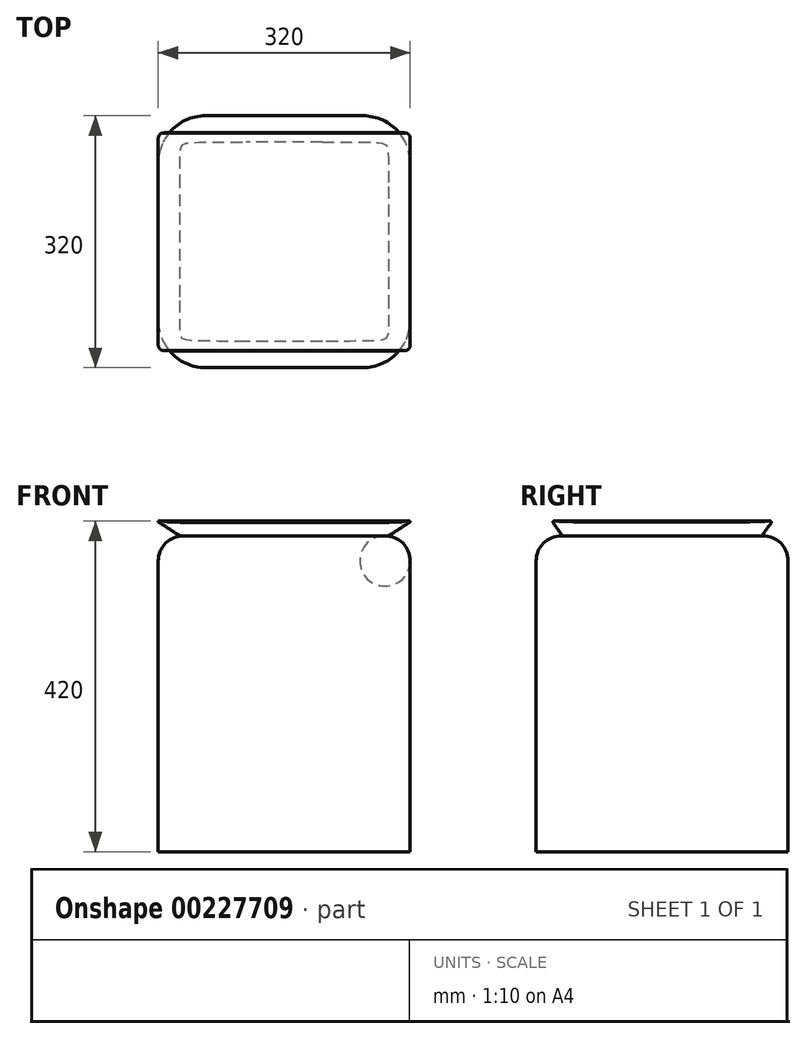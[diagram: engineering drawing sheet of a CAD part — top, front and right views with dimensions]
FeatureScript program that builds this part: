
annotation { "Feature Type Name" : "Feature", "Feature Type Description" : "" }
export const myFeature = defineFeature(function(context is Context, id is Id, definition is map)
    precondition{}
    {
        {
            var Q0;
            Q0=qCreatedBy(makeId("Right.planeOp"),FACE);
            var sketch = newSketch(context, id + "F0", { "sketchPlane" : qUnion([Q0])});
            skLineSegment(sketch, "E0", {"start": v(-172.62, -274.52) * mm, "end": v(-172.62, 126.84) * mm});
            skLineSegment(sketch, "E1", {"start": v(-172.62, 126.84) * mm, "end": v(-139.2, 126.84) * mm});
            skLineSegment(sketch, "E2", {"start": v(-139.2, 126.84) * mm, "end": v(-152.62, 108.2) * mm});
            skLineSegment(sketch, "E3", {"start": v(-152.62, 108.2) * mm, "end": v(127.38, 108.2) * mm});
            skLineSegment(sketch, "E4", {"start": v(127.38, 108.2) * mm, "end": v(113.96, 126.84) * mm});
            skLineSegment(sketch, "E5", {"start": v(113.96, 126.84) * mm, "end": v(147.38, 126.84) * mm});
            skLineSegment(sketch, "E6", {"start": v(147.38, 126.84) * mm, "end": v(147.38, -274.52) * mm});
            skLineSegment(sketch, "E7", {"start": v(147.38, -274.52) * mm, "end": v(-172.62, -274.52) * mm});
            skLineSegment(sketch, "E8", {"start": v(-12.62, 108.2) * mm, "end": v(-12.62, -274.52) * mm, "construction": true});
            skLineSegment(sketch, "E9", {"start": v(-139.2, 126.84) * mm, "end": v(113.96, 126.84) * mm});
            skLineSegment(sketch, "E10.MirrorCS", {"start": v(127.38, 145.48) * mm, "end": v(113.96, 126.84) * mm});
            skLineSegment(sketch, "E11.MirrorCS", {"start": v(-139.2, 126.84) * mm, "end": v(-152.62, 145.48) * mm});
            skLineSegment(sketch, "E12.MirrorCS", {"start": v(-152.62, 145.48) * mm, "end": v(127.38, 145.48) * mm});
            skSolve(sketch);
        }
        {
            var Q0;
            Q0=makeQuery(id+"F0.imprint","IMPRINT",FACE,{"disambiguationData":[TD([[makeQuery(id+"F0.imprint","IMPRINT",EDGE,{"derivedFrom":sQuery(id+"F0.wireOp",EDGE,"E0")}),-1.0]])]});
            var Q1;
            Q1=makeQuery(id+"F0.imprint","IMPRINT",FACE,{"disambiguationData":[TD([[makeQuery(id+"F0.imprint","IMPRINT",EDGE,{"derivedFrom":sQuery(id+"F0.wireOp",EDGE,"E2")}),1.0]])]});
            extrude(context, id + "F1", {"entities" : qUnion([Q0, Q1]), "depth" : 320 * mm, "symmetric" : true});
        }
        {
            var Q0;
            Q0=makeQuery(id+"F0.imprint","IMPRINT",FACE,{"disambiguationData":[TD([[makeQuery(id+"F0.imprint","IMPRINT",EDGE,{"derivedFrom":sQuery(id+"F0.wireOp",EDGE,"E9")}),1.0]])]});
            extrude(context, id + "F2", {"entities" : qUnion([Q0]), "depth" : 320 * mm, "symmetric" : true});
        }
        {
            var Q0;
            Q0=makeQuery(id+"F1.opExtrude","CAP_EDGE",EDGE,{"disambiguationData":[OSD([sQuery(id+"F0.wireOp",EDGE,"E6")])],"isStart":false});
            var Q1;
            Q1=makeQuery(id+"F1.opExtrude","CAP_EDGE",EDGE,{"disambiguationData":[OSD([sQuery(id+"F0.wireOp",EDGE,"E6")])],"isStart":true});
            var Q2;
            Q2=makeQuery(id+"F1.opExtrude","CAP_EDGE",EDGE,{"disambiguationData":[OSD([sQuery(id+"F0.wireOp",EDGE,"E0")])],"isStart":false});
            var Q3;
            Q3=makeQuery(id+"F1.opExtrude","CAP_EDGE",EDGE,{"disambiguationData":[OSD([sQuery(id+"F0.wireOp",EDGE,"E0")])],"isStart":true});
            fillet(context, id + "F3", {"entities" : qUnion([Q0, Q1, Q2, Q3]), "radius" : 60 * mm, "tangentPropagation" : true, "allowEdgeOverflow" : false});
        }
        {
            var Q0;
            Q0=makeQuery(id+"F1.opExtrude","SWEPT_EDGE",EDGE,{"disambiguationData":[OSD([sQuery(id+"F0.wireOp",EDGE,"E5"),sQuery(id+"F0.wireOp",EDGE,"E6")])]});
            var Q1;
            Q1=makeQuery(id+"F1.opExtrude","SWEPT_EDGE",EDGE,{"disambiguationData":[OSD([sQuery(id+"F0.wireOp",EDGE,"E0"),sQuery(id+"F0.wireOp",EDGE,"E1")])]});
            var Q2;
            Q2=makeQuery(id+"F1.opExtrude","CAP_EDGE",EDGE,{"disambiguationData":[OSD([sQuery(id+"F0.wireOp",EDGE,"E5")])],"isStart":false});
            var Q3;
            Q3=makeQuery(id+"F1.opExtrude","CAP_EDGE",EDGE,{"disambiguationData":[OSD([sQuery(id+"F0.wireOp",EDGE,"E1")])],"isStart":false});
            var Q4;
            Q4=makeQuery(id+"F1.opExtrude","CAP_EDGE",EDGE,{"disambiguationData":[OSD([sQuery(id+"F0.wireOp",EDGE,"E5")])],"isStart":true});
            var Q5;
            Q5=makeQuery(id+"F1.opExtrude","CAP_EDGE",EDGE,{"disambiguationData":[OSD([sQuery(id+"F0.wireOp",EDGE,"E1")])],"isStart":true});
            fillet(context, id + "F4", {"entities" : qUnion([Q0, Q1, Q2, Q3, Q4, Q5]), "radius" : 32 * mm, "tangentPropagation" : true, "allowEdgeOverflow" : false});
        }
        {
            var Q0;
            Q0=makeQuery(id+"F2.opExtrude","SWEPT_EDGE",EDGE,{"disambiguationData":[OSD([sQuery(id+"F0.wireOp",EDGE,"E10.MirrorCS"),sQuery(id+"F0.wireOp",EDGE,"E12.MirrorCS")])]});
            var Q1;
            Q1=makeQuery(id+"F2.opExtrude","SWEPT_EDGE",EDGE,{"disambiguationData":[OSD([sQuery(id+"F0.wireOp",EDGE,"E11.MirrorCS"),sQuery(id+"F0.wireOp",EDGE,"E12.MirrorCS")])]});
            chamfer(context, id + "F5", {"entities" : qUnion([Q0, Q1]), "width" : 1 * mm, "tangentPropagation" : true});
        }
        {
            var Q0;
            Q0=makeQuery(id+"F2.opExtrude","CAP_EDGE",EDGE,{"disambiguationData":[OSD([sQuery(id+"F0.wireOp",EDGE,"E9")])],"isStart":false});
            var Q1;
            Q1=makeQuery(id+"F2.opExtrude","CAP_EDGE",EDGE,{"disambiguationData":[OSD([sQuery(id+"F0.wireOp",EDGE,"E9")])],"isStart":true});
            chamfer(context, id + "F6", {"entities" : qUnion([Q0, Q1]), "chamferType" : ChamferType.OFFSET_ANGLE, "width" : 17.8 * mm, "oppositeDirection" : false, "angle" : 57 * degree, "tangentPropagation" : true});
        }
        {
            var Q0;
            Q0=makeQuery(id+"F2.opExtrude","SWEPT_FACE",FACE,{"disambiguationData":[OSD([sQuery(id+"F0.wireOp",EDGE,"E12.MirrorCS")])]});
            var sketch = newSketch(context, id + "F7", { "sketchPlane" : qUnion([Q0])});
            skLineSegment(sketch, "E13.0.0", {"start": v(-160, 126.38) * mm, "end": v(-160, -151.62) * mm});
            skLineSegment(sketch, "E13.0.1", {"start": v(-160, -151.62) * mm, "end": v(160, -151.62) * mm});
            skLineSegment(sketch, "E13.0.2", {"start": v(160, -151.62) * mm, "end": v(160, 126.38) * mm});
            skLineSegment(sketch, "E13.0.3", {"start": v(160, 126.38) * mm, "end": v(-160, 126.38) * mm});
            skSolve(sketch);
        }
        {
            var Q0;
            Q0=makeQuery(id+"F1.opExtrude","SWEPT_FACE",FACE,{"disambiguationData":[OSD([sQuery(id+"F0.wireOp",EDGE,"E1"),sQuery(id+"F0.wireOp",EDGE,"E5"),sQuery(id+"F0.wireOp",EDGE,"E9")])]});
            var sketch = newSketch(context, id + "F8", { "sketchPlane" : qUnion([Q0])});
            skArc(sketch, "E14.0.0", {"start": v(100, -140.62) * mm, "mid": v(119.8, -132.42) * mm, "end": v(128, -112.62) * mm});
            skLineSegment(sketch, "E14.0.1", {"start": v(128, -112.62) * mm, "end": v(128, 87.38) * mm});
            skArc(sketch, "E14.0.2", {"start": v(128, 87.38) * mm, "mid": v(119.8, 107.18) * mm, "end": v(100, 115.38) * mm});
            skLineSegment(sketch, "E14.0.3", {"start": v(100, 115.38) * mm, "end": v(-100, 115.38) * mm});
            skArc(sketch, "E14.0.4", {"start": v(-100, 115.38) * mm, "mid": v(-119.8, 107.18) * mm, "end": v(-128, 87.38) * mm});
            skLineSegment(sketch, "E14.0.5", {"start": v(-128, 87.38) * mm, "end": v(-128, -112.62) * mm});
            skArc(sketch, "E14.0.6", {"start": v(-128, -112.62) * mm, "mid": v(-119.8, -132.42) * mm, "end": v(-100, -140.62) * mm});
            skLineSegment(sketch, "E14.0.7", {"start": v(-100, -140.62) * mm, "end": v(100, -140.62) * mm});
            skSolve(sketch);
        }
        {
            var Q0;
            Q0=sQuery(id+"F8.wireOp",EDGE,"E14.0.0");
            cPoint(context, id + "F9", {"entities" : qUnion([Q0]), "parameter" : 0.5});
        }
        {
            var Q0;
            Q0 = qCreatedBy(id + "F9" ,VERTEX);
            var Q1;
            Q1=sQuery(id+"F7.wireOp",VERTEX,"E13.0.2.start");
            var Q2;
            Q2=sQuery(id+"F7.wireOp",VERTEX,"E13.0.0.start");
            cPlane(context, id + "F10", {"entities" : qUnion([Q0, Q1, Q2]), "cplaneType" : CPlaneType.THREE_POINT, "offset" : 25 * mm, "width" : 150 * mm, "height" : 150 * mm});
        }
        {
            var Q0;
            Q0=makeQuery(id+"F6.opChamfer","BLEND_EDGE",EDGE,{"blendedFrom":[makeQuery(id+"F2.opExtrude","CAP_EDGE",EDGE,{"disambiguationData":[OSD([sQuery(id+"F0.wireOp",EDGE,"E9")])],"isStart":false}),makeQuery(id+"F2.opExtrude","SWEPT_FACE",FACE,{"disambiguationData":[OSD([sQuery(id+"F0.wireOp",EDGE,"E11.MirrorCS")])]})],"blendedInto":[makeQuery(id+"F2.opExtrude","SWEPT_FACE",FACE,{"disambiguationData":[OSD([sQuery(id+"F0.wireOp",EDGE,"E11.MirrorCS")])]})]});
            var Q1;
            Q1=makeQuery(id+"F6.opChamfer","BLEND_EDGE",EDGE,{"blendedFrom":[makeQuery(id+"F2.opExtrude","CAP_EDGE",EDGE,{"disambiguationData":[OSD([sQuery(id+"F0.wireOp",EDGE,"E9")])],"isStart":false}),makeQuery(id+"F2.opExtrude","SWEPT_FACE",FACE,{"disambiguationData":[OSD([sQuery(id+"F0.wireOp",EDGE,"E10.MirrorCS")])]})],"blendedInto":[makeQuery(id+"F2.opExtrude","SWEPT_FACE",FACE,{"disambiguationData":[OSD([sQuery(id+"F0.wireOp",EDGE,"E10.MirrorCS")])]})]});
            var Q2;
            Q2=makeQuery(id+"F6.opChamfer","BLEND_EDGE",EDGE,{"blendedFrom":[makeQuery(id+"F2.opExtrude","CAP_EDGE",EDGE,{"disambiguationData":[OSD([sQuery(id+"F0.wireOp",EDGE,"E9")])],"isStart":true}),makeQuery(id+"F2.opExtrude","SWEPT_FACE",FACE,{"disambiguationData":[OSD([sQuery(id+"F0.wireOp",EDGE,"E10.MirrorCS")])]})],"blendedInto":[makeQuery(id+"F2.opExtrude","SWEPT_FACE",FACE,{"disambiguationData":[OSD([sQuery(id+"F0.wireOp",EDGE,"E10.MirrorCS")])]})]});
            var Q3;
            Q3=makeQuery(id+"F6.opChamfer","BLEND_EDGE",EDGE,{"blendedFrom":[makeQuery(id+"F2.opExtrude","CAP_EDGE",EDGE,{"disambiguationData":[OSD([sQuery(id+"F0.wireOp",EDGE,"E9")])],"isStart":true}),makeQuery(id+"F2.opExtrude","SWEPT_FACE",FACE,{"disambiguationData":[OSD([sQuery(id+"F0.wireOp",EDGE,"E11.MirrorCS")])]})],"blendedInto":[makeQuery(id+"F2.opExtrude","SWEPT_FACE",FACE,{"disambiguationData":[OSD([sQuery(id+"F0.wireOp",EDGE,"E11.MirrorCS")])]})]});
            fillet(context, id + "F11", {"entities" : qUnion([Q0, Q1, Q2, Q3]), "radius" : 90 * mm, "tangentPropagation" : true, "rho" : 0.9, "crossSection" : FilletCrossSection.CONIC, "allowEdgeOverflow" : false});
        }
    });
